# Revit family: Rio 190 0-10V
name_source: partatom
category: Lighting Fixtures
revit_build: Autodesk Revit 2018 (Build: 20170927_1515(x64)
units: mm (PartAtom-declared; Revit-internal decimal feet)

## family parameters
Always vertical = Yes
Cut with Voids When Loaded = No
Host = Wall
Light Source = Yes
OmniClass Number = 23.80.70.00
OmniClass Title = Lighting
Part Type = Normal
Room Calculation Point = No
Round Connector Dimension = Use Diameter
Shared = No

## types (2) — shared parameters
Color Filter = 16777215
Dimming Lamp Color Temperature Shift = <None>
Driver Required = No
Emit from Line Length = 610 mm
Manufacturer = Astro Lighting Ltd
URL = www.astrolighting.com

## per-type parameters (varying)
| type | ADA compliant | Apparent Load | Dimmable | Dimming Method | Driver Included | Efficacy (lm/w) | Electrical Class | Lamp | Light Source Fixed | Location rating | Main Finish | Main Material | Photometric Web File | Power (Watts) | Product Code | Product Location | Product Name | Product SKU | Tilt Angle |
| CE |  | 0 VA |  |  |  |  | 0 |  |  |  |  | Metal - Steel | generic |  | 1234 |  |  | 1234001 | 60.00° |
| ETL | Yes | 14 VA | Yes | 0-10V | Yes | 99 | 1 | LED | Yes | Dry | Plaster | Plaster | GNC-20558 8479 Rio 190 LED 0_1-10V IES.ies | 14.0 | 8479 | Indoor | Rio 190 0-10V | 1325014 | 0.00° |

## geometry (parser evidence)
native form markers: Sweep x1
no freeform markers — native parametric forms only
